# Revit family: Reece_Basin_Wolfen_Wall Basin_600 mm
name_source: partatom
category: Plumbing Fixtures
revit_build: Autodesk Revit 2018 (Build: 20190510_1515(x64)
units: mm (PartAtom-declared; Revit-internal decimal feet)

## family parameters
Always vertical = Yes
Cut with Voids When Loaded = Yes
Part Type = Normal
Room Calculation Point = Yes
Round Connector Dimension = Use Diameter
Shared = Yes
Work Plane-Based = Yes

## types (1)
- 12 L_1 Taphole_Centre Bowl_Vitreous China
    Default Elevation = 0 mm  [stored 0 ft]
    Description = Wolfen Wall Basin 600 x 480 x 205mm with Overflow & fixings 1 Taphole White
    Disclaimer = THIS FILE IS THE PROPERTY OF THE REECE GROUP. IT MAY NOT BE REPRODUCED, REVERSE-ENGINEERED OR MODIFIED. ANY REPUBLICATION, TRANSMISSION OR DISTRIBUTION FOR THE PURPOSE OF COMMERCIALLY EXPLOITING THE FILES IS PROHIBITED.
    Keynote = Product #1851596, Reece_Basin_Wolfen_Wall Basin_600 mm - 12 L_1 Taphole_Centre Bowl_Vitreous China
    Manufacturer = Wolfen
    Model = Wolfen
    Reece_Basin_Outlet = 40 mm  [stored 0.131234 ft]
    Reece_Detail_Additional = With Fixings and Overflow
    Reece_Detail_Bowl Type = Centre Bowl
    Reece_Detail_Disclaimer = THIS FILE IS THE PROPERTY OF THE REECE GROUP. IT MAY NOT BE REPRODUCED, REVERSE-ENGINEERED OR MODIFIED. ANY REPUBLICATION, TRANSMISSION OR DISTRIBUTION FOR THE PURPOSE OF COMMERCIALLY EXPLOITING THE FILES IS PROHIBITED.
    Reece_Detail_Taphole Configuration = 1 Taphole
    Reece_Material_Main = Reece_Vitreous China_White
    Reece_Material_Secondary = Reece_Brass_Chrome
    Reece_Overall_Capacity = 12 L
    Reece_Overall_Depth = 480 mm  [stored 1.5748 ft]
    Reece_Overall_Height = 205 mm  [stored 0.672572 ft]
    Reece_Overall_Width = 600 mm
    Reece_Product_Brand = Wolfen
    Reece_Product_Description = Wolfen Wall Basin 600 x 480 x 205mm with Overflow & fixings 1 Taphole White
    Reece_Product_Mount = Wall Mounted
    Reece_Product_Number = 1851596
    Reece_Product_Sub Brand = Wolfen
    Reece_Product_Type = Basin
    Reece_Product_Web Page = https://www.reece.com.au
    Type Comments = Basin
    URL = https://www.reece.com.au

note: [stored X ft] marks values corroborated as IEEE doubles in the binary element streams (Revit-internal decimal feet)

## geometry (parser evidence)
native form markers: Sweep x6
no freeform markers — native parametric forms only
